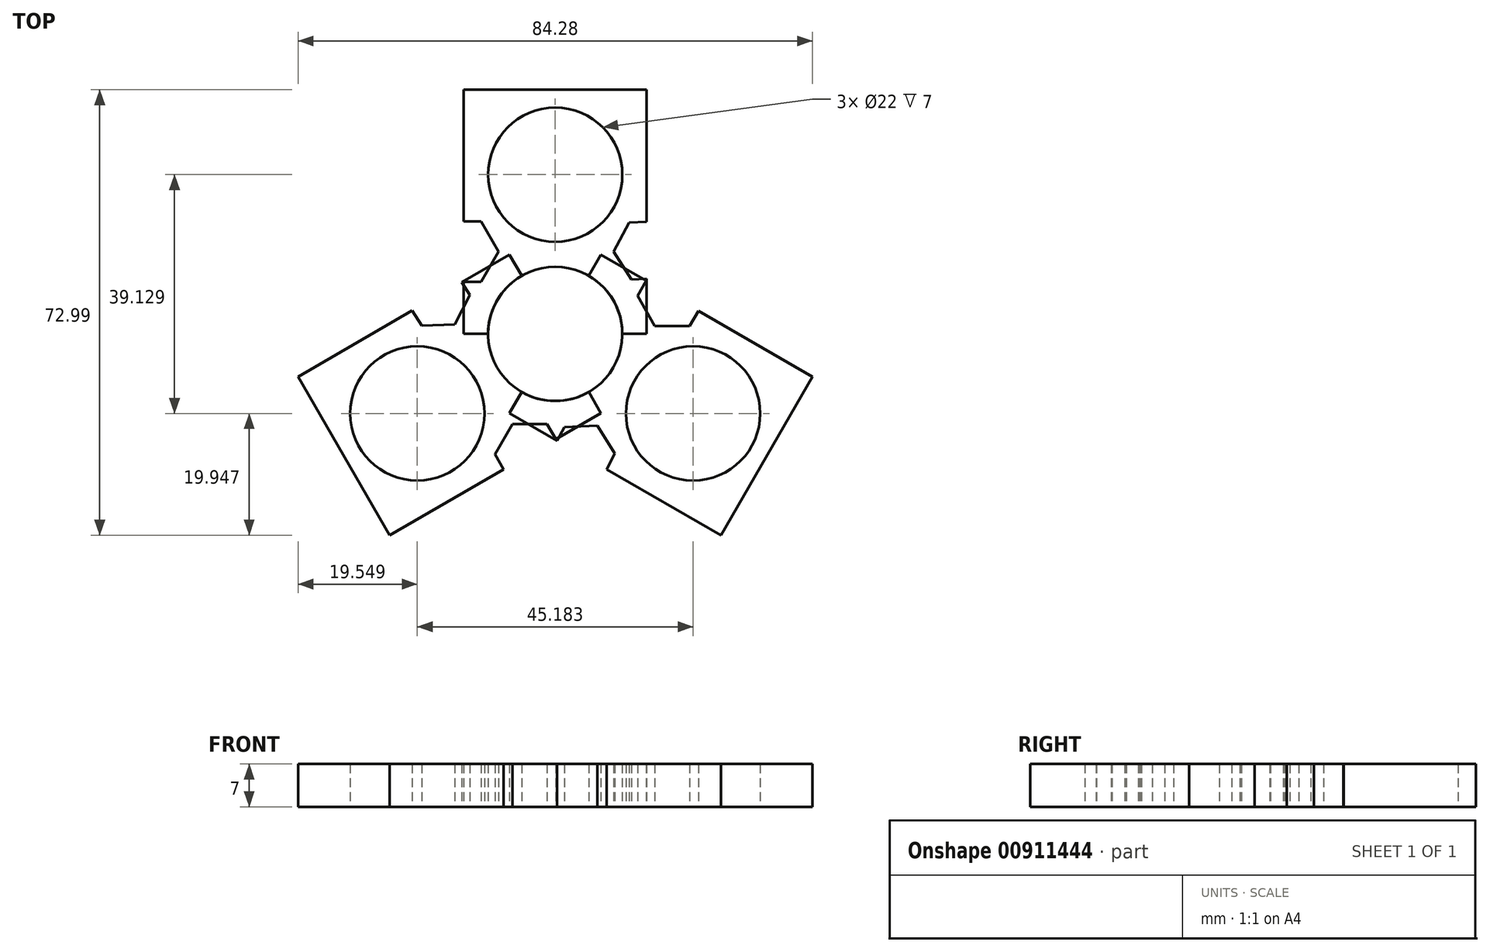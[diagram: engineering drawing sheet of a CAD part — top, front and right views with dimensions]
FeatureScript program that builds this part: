
annotation { "Feature Type Name" : "Feature", "Feature Type Description" : "" }
export const myFeature = defineFeature(function(context is Context, id is Id, definition is map)
    precondition{}
    {
        {
            var Q0;
            Q0=qCreatedBy(makeId("Top.planeOp"),FACE);
            var sketch = newSketch(context, id + "F0", { "sketchPlane" : qUnion([Q0])});
            skCircle(sketch, "E0", {"center": v(0, 0) * mm, "radius": 11 * mm});
            skLineSegment(sketch, "E1.bottom", {"start": v(0, 0) * mm, "end": v(15, 0) * mm});
            skLineSegment(sketch, "E1.top", {"start": v(0, 40) * mm, "end": v(15, 40) * mm});
            skLineSegment(sketch, "E1.left", {"start": v(0, 0) * mm, "end": v(0, 40) * mm});
            skLineSegment(sketch, "E1.right", {"start": v(15, 0) * mm, "end": v(15, 40) * mm});
            skLineSegment(sketch, "E2.bottom", {"start": v(0, 0) * mm, "end": v(-15, 0) * mm});
            skLineSegment(sketch, "E2.top", {"start": v(0, 40) * mm, "end": v(-15, 40) * mm});
            skLineSegment(sketch, "E2.right", {"start": v(-15, 0) * mm, "end": v(-15, 40) * mm});
            skLineSegment(sketch, "E3", {"start": v(0, 40) * mm, "end": v(0, 26.09) * mm});
            skCircle(sketch, "E4", {"center": v(0, 26.09) * mm, "radius": 11 * mm});
            skCircle(sketch, "E5.cCircle", {"center": v(15, 13.7) * mm, "radius": 4.68 * mm, "construction": true});
            skLineSegment(sketch, "E5.0", {"start": v(20.4, 13.91) * mm, "end": v(17.89, 9.13) * mm});
            skLineSegment(sketch, "E5.1", {"start": v(17.89, 9.13) * mm, "end": v(12.49, 8.92) * mm});
            skLineSegment(sketch, "E5.2", {"start": v(12.49, 8.92) * mm, "end": v(9.6, 13.48) * mm});
            skLineSegment(sketch, "E5.3", {"start": v(9.6, 13.48) * mm, "end": v(12.11, 18.27) * mm});
            skLineSegment(sketch, "E5.4", {"start": v(12.11, 18.27) * mm, "end": v(17.51, 18.48) * mm});
            skLineSegment(sketch, "E5.5", {"start": v(17.51, 18.48) * mm, "end": v(20.4, 13.91) * mm});
            skPoint(sketch, "E5.0.midPoint", {"position": v(19.14, 11.52) * mm});
            skCircle(sketch, "E6.cCircle", {"center": v(-15, 13.48) * mm, "radius": 4.93 * mm, "construction": true});
            skLineSegment(sketch, "E6.0", {"start": v(-17.85, 18.42) * mm, "end": v(-12.15, 18.42) * mm});
            skLineSegment(sketch, "E6.1", {"start": v(-12.15, 18.42) * mm, "end": v(-9.3, 13.48) * mm});
            skLineSegment(sketch, "E6.2", {"start": v(-9.3, 13.48) * mm, "end": v(-12.15, 8.55) * mm});
            skLineSegment(sketch, "E6.3", {"start": v(-12.15, 8.55) * mm, "end": v(-17.85, 8.55) * mm});
            skLineSegment(sketch, "E6.4", {"start": v(-17.85, 8.55) * mm, "end": v(-20.7, 13.48) * mm});
            skLineSegment(sketch, "E6.5", {"start": v(-20.7, 13.48) * mm, "end": v(-17.85, 18.42) * mm});
            skPoint(sketch, "E6.0.midPoint", {"position": v(-15, 18.42) * mm});
            skSolve(sketch);
        }
        {
            var Q0;
            {var subQ9=sQuery(id+"F0.wireOp",EDGE,"E1.top");Q0=makeQuery(id+"F0.imprint","IMPRINT",FACE,{"disambiguationData":[TD([[makeQuery(id+"F0.imprint","IMPRINT",EDGE,{"derivedFrom":subQ9}),-1.0]])]});}
            var Q1;
            {var subQ0=sQuery(id+"F0.wireOp",EDGE,"E2.top");Q1=makeQuery(id+"F0.imprint","IMPRINT",FACE,{"disambiguationData":[TD([[makeQuery(id+"F0.imprint","IMPRINT",EDGE,{"derivedFrom":subQ0}),1.0]])]});}
            extrude(context, id + "F1", {"entities" : qUnion([Q0, Q1]), "depth" : 7 * mm, "offsetDistance" : 25 * mm});
        }
        {
            var Q0;
            Q0=qCreatedBy(makeId("Front.planeOp"),FACE);
            var sketch = newSketch(context, id + "F2", { "sketchPlane" : qUnion([Q0])});
            skLineSegment(sketch, "E7", {"start": v(0, 0) * mm, "end": v(0, 46.18) * mm});
            skSolve(sketch);
        }
        {
            var Q0;
            Q0=makeQuery(id+"F1.opExtrude","SWEPT_BODY",BODY,{"disambiguationData":[OSD([sQuery(id+"F0.wireOp",EDGE,"E0"),sQuery(id+"F0.wireOp",EDGE,"E1.bottom"),sQuery(id+"F0.wireOp",EDGE,"E1.top"),sQuery(id+"F0.wireOp",EDGE,"E1.right"),sQuery(id+"F0.wireOp",EDGE,"E2.bottom"),sQuery(id+"F0.wireOp",EDGE,"E2.top"),sQuery(id+"F0.wireOp",EDGE,"E2.right"),sQuery(id+"F0.wireOp",EDGE,"E4")])]});
            var Q1;
            Q1=sQuery(id+"F2.wireOp",EDGE,"E7");
            transform(context, id + "F3", {"entities" : qUnion([Q0]), "transformType" : TransformType.ROTATION, "transformAxis" : qUnion([Q1]), "angle" : 120 * degree, "makeCopy" : true});
        }
        {
            var Q0;
            Q0=makeQuery(id+"F1.opExtrude","SWEPT_BODY",BODY,{"disambiguationData":[OSD([sQuery(id+"F0.wireOp",EDGE,"E0"),sQuery(id+"F0.wireOp",EDGE,"E1.bottom"),sQuery(id+"F0.wireOp",EDGE,"E1.top"),sQuery(id+"F0.wireOp",EDGE,"E1.right"),sQuery(id+"F0.wireOp",EDGE,"E2.bottom"),sQuery(id+"F0.wireOp",EDGE,"E2.top"),sQuery(id+"F0.wireOp",EDGE,"E2.right"),sQuery(id+"F0.wireOp",EDGE,"E4")])]});
            var Q1;
            Q1=sQuery(id+"F2.wireOp",EDGE,"E7");
            transform(context, id + "F4", {"entities" : qUnion([Q0]), "transformType" : TransformType.ROTATION, "transformAxis" : qUnion([Q1]), "angle" : 240 * degree, "makeCopy" : true});
        }
    });
